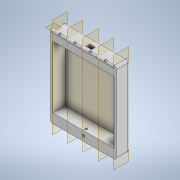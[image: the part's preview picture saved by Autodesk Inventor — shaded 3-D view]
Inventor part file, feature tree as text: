
AUTODESK INVENTOR PART (.ipt)
format: ipt  version: 2022 (Build 260153000, 153)  size: 322,048 bytes
history: native  units: in
note: dims shown in document units (in); Inventor stores cm internally (conversion verified against a paired STEP export)
features: extrude x14, sketch x14, plane x7, projected_geometry x4, fillet x3
ambient origin geometry x8: Origin, YZ Plane, XZ Plane, XY Plane, X Axis, Y Axis, Z Axis, Center Point
bodies: Solid1 (feature_tree)
feature tree (42):
  extrude  "Extrusion1"  Depth=1.0in
  extrude  "Extrusion3"  Depth=0.25in
  fillet  "Fillet1"  Radius=0.25in
  plane  "Work Plane1"
  plane  "Work Plane5"
  plane  "Work Plane6"
  extrude  "Extrusion9"  Depth=1.48in TaperAngle=0.0deg
  extrude  "Extrusion10"  Depth=0.25in
  extrude  "Extrusion11"  Depth=0.297in
  extrude  "Extrusion12"  Depth=0.317in
  extrude  "Extrusion14"  Depth=0.25in
  extrude  "Extrusion15"  Depth=0.541in
  plane  "Work Plane7"
  extrude  "Extrusion16"  Depth=0.413in
  extrude  "Extrusion17"  Depth=3.0in TaperAngle=0.0deg
  plane  "Work Plane11"
  extrude  "Extrusion20"  Depth=0.1in TaperAngle=0.0deg
  extrude  "Extrusion21"  Depth=0.25in
  extrude  "Extrusion22"  Depth=0.125in
  fillet  "Fillet4"  Radius=0.8125in
  extrude  "Extrusion23"  Depth=0.2in
  fillet  "Fillet5"  Radius=6.5in
  sketch  "Sketch1"  dims[d0=6.506in d2=1.0in]
  sketch  "Sketch3"  dims[d3=1.0in d4=0.25in d5=0.25in]
  sketch  "Sketch10"  dims[d6=1.48in d7=0.0in d10=0.185in d11=0.0in]
  projected_geometry  "Projected Loop1"
  sketch  "Sketch11"  dims[d12=0.25in d13=0.01in]
  projected_geometry  "Projected Loop2"
  sketch  "Sketch13"  dims[d43=0.225in d44=0.0in d47=0.297in]
  sketch  "Sketch14"  dims[d48=4.0in d49=0.0in d50=0.317in]
  sketch  "Sketch17"  dims[d51=1.313in d52=0.0in d53=0.25in]
  projected_geometry  "Projected Loop6"
  sketch  "Sketch18"  dims[d54=0.75in d55=0.0in d63=0.541in]
  sketch  "Sketch19"  dims[d64=0.2935in d65=0.413in]
  sketch  "Sketch20"  dims[d66=0.6in d67=3.0in d68=0.0in]
  plane  "Work Plane9"
  plane  "Work Plane10"
  sketch  "Sketch23"  dims[d69=0.5in d70=0.1in d71=0.0in]
  sketch  "Sketch24"  dims[d72=6.5in d73=0.25in]
  sketch  "Sketch25"  dims[d74=0.25in d75=0.125in d76=0.8125in d77=0.0in]
  sketch  "Sketch26"  dims[d78=0.3in d79=0.2in d80=6.5in d81=0.0in d93=1.625in d94=1.625in d95=1.625in d96=0.25in d97=0.25in d98=0.125in d99=0.8125in d100=0.0in d101=0.25in d102=0.25in d103=0.125in d104=0.8125in d105=0.0in d106=0.25in d107=0.25in d108=0.125in d109=0.8125in d110=0.0in d111=0.125in d112=0.125in d113=0.0in d114=0.125in d41=0.5in d42=0.0344in]
  projected_geometry  "Projected Loop7"
